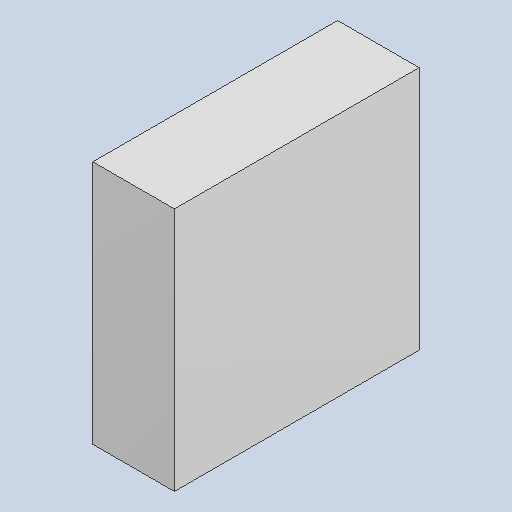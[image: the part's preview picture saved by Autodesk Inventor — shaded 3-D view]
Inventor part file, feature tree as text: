
AUTODESK INVENTOR PART (.ipt)
format: ipt  version: 2023.4 (Build 274418000, 418)  size: 81,408 bytes
history: native  units: mm
features: extrude x1
ambient origin geometry x8: Origin, YZ Plane, XZ Plane, XY Plane, X Axis, Y Axis, Z Axis, Center Point
bodies: Solid1 (feature_tree)
feature tree (1):
  extrude  "Extruded_31"  [1 undecoded]
note: 1 required parameter value undecoded (feature->parameter linkage not recoverable at this tier; creation-order binding heuristic only, values carry confidence <= 0.55)
